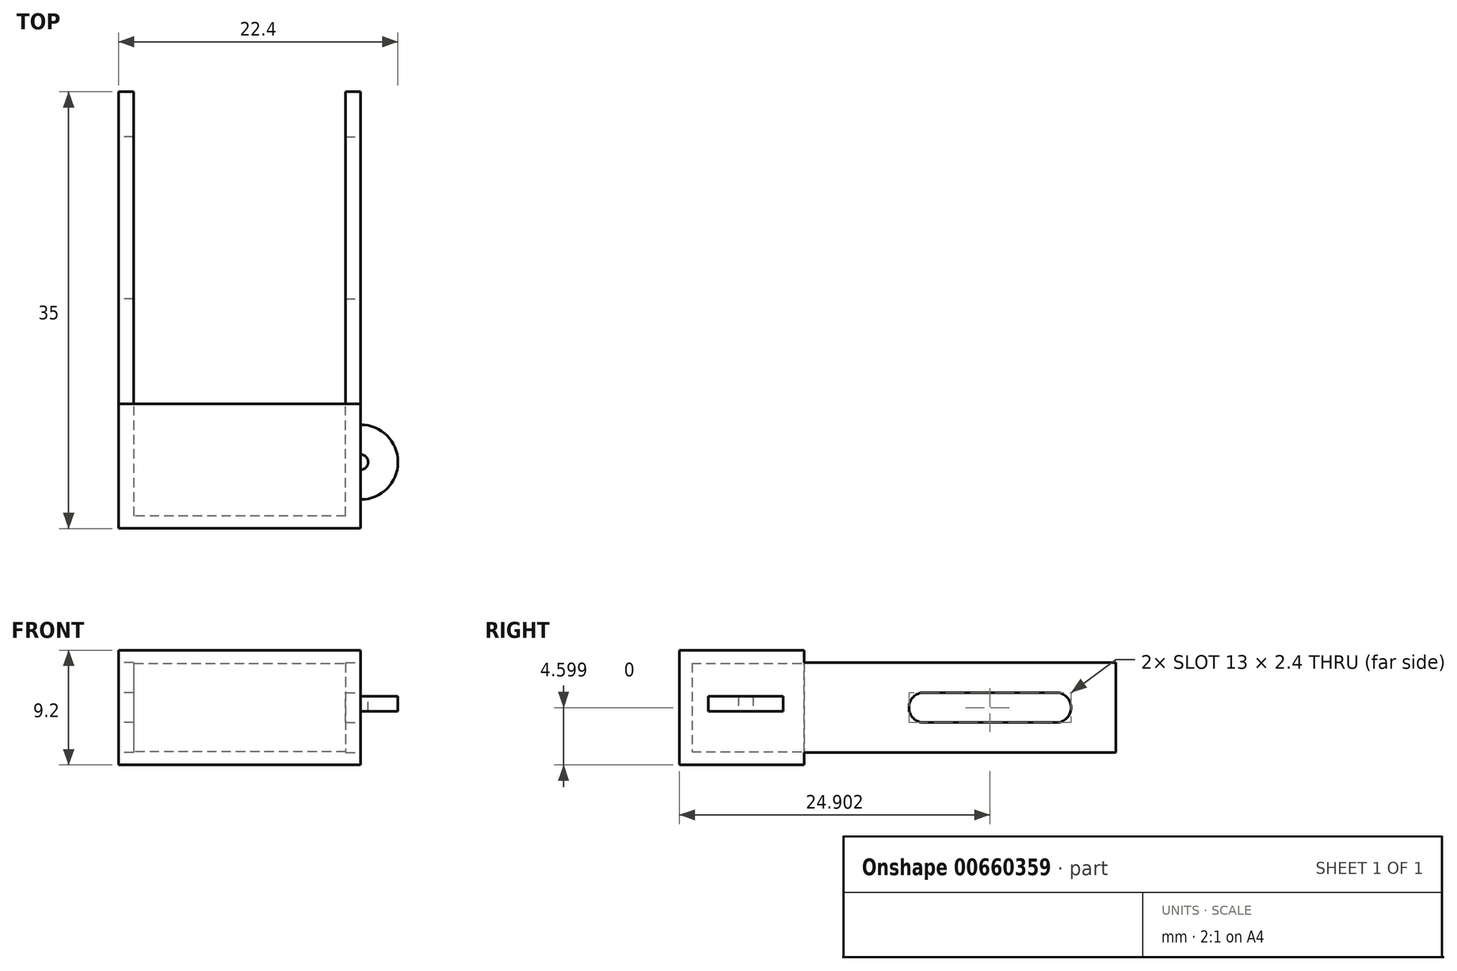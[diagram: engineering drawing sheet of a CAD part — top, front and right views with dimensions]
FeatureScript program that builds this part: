
annotation { "Feature Type Name" : "Feature", "Feature Type Description" : "" }
export const myFeature = defineFeature(function(context is Context, id is Id, definition is map)
    precondition{}
    {
        {
            var Q0;
            Q0=qCreatedBy(makeId("Right.planeOp"),FACE);
            var sketch = newSketch(context, id + "F0", { "sketchPlane" : qUnion([Q0])});
            skLineSegment(sketch, "E0.bottom", {"start": v(-18.67, 6.84) * mm, "end": v(-8.67, 6.84) * mm});
            skLineSegment(sketch, "E0.top", {"start": v(-18.67, -2.36) * mm, "end": v(-8.67, -2.36) * mm});
            skLineSegment(sketch, "E0.left", {"start": v(-18.67, 6.84) * mm, "end": v(-18.67, -2.36) * mm});
            skLineSegment(sketch, "E0.right", {"start": v(-8.67, 6.84) * mm, "end": v(-8.67, -2.36) * mm});
            skPoint(sketch, "E1", {"position": v(-8.67, 2.24) * mm});
            skLineSegment(sketch, "E2", {"start": v(-8.67, 2.24) * mm, "end": v(-8.67, 5.84) * mm});
            skLineSegment(sketch, "E3", {"start": v(-8.67, 5.84) * mm, "end": v(16.33, 5.84) * mm});
            skLineSegment(sketch, "E4", {"start": v(16.33, 5.84) * mm, "end": v(16.33, -1.36) * mm});
            skLineSegment(sketch, "E5", {"start": v(16.33, -1.36) * mm, "end": v(-8.67, -1.36) * mm});
            skLineSegment(sketch, "E6.top", {"start": v(-8.67, -1.36) * mm, "end": v(16.33, -1.36) * mm});
            skLineSegment(sketch, "E6.left", {"start": v(-8.67, 6.84) * mm, "end": v(-8.67, -1.36) * mm});
            skPoint(sketch, "E7", {"position": v(11.53, 2.24) * mm});
            skPoint(sketch, "E8", {"position": v(0.93, 2.24) * mm});
            skArc(sketch, "E9", {"start": v(11.53, 1.04) * mm, "mid": v(12.73, 2.24) * mm, "end": v(11.53, 3.44) * mm});
            skArc(sketch, "E10", {"start": v(0.93, 3.44) * mm, "mid": v(-0.27, 2.24) * mm, "end": v(0.93, 1.04) * mm});
            skLineSegment(sketch, "E11", {"start": v(0.93, 3.44) * mm, "end": v(11.53, 3.44) * mm});
            skLineSegment(sketch, "E12", {"start": v(11.53, 1.04) * mm, "end": v(0.93, 1.04) * mm});
            skSolve(sketch);
        }
        {
            var Q0;
            {var subQ1=sQuery(id+"F0.wireOp",EDGE,"E0.bottom");Q0=makeQuery(id+"F0.imprint","IMPRINT",FACE,{"disambiguationData":[TD([[makeQuery(id+"F0.imprint","IMPRINT",EDGE,{"derivedFrom":subQ1}),-1.0]])]});}
            extrude(context, id + "F1", {"entities" : qUnion([Q0]), "depth" : 19.4 * mm, "offsetDistance" : 25 * mm});
        }
        {
            var Q0;
            Q0=qSketchRegion(id+"F0",true);
            extrude(context, id + "F2", {"entities" : qUnion([Q0]), "operationType" : NewBodyOperationType.ADD, "depth" : 1.2 * mm, "offsetDistance" : 25 * mm});
        }
        {
            var Q0;
            Q0=makeQuery(id+"F1.opExtrude","CAP_FACE",FACE,{"disambiguationData":[OSD([sQuery(id+"F0.wireOp",EDGE,"E0.bottom"),sQuery(id+"F0.wireOp",EDGE,"E0.top"),sQuery(id+"F0.wireOp",EDGE,"E0.left"),sQuery(id+"F0.wireOp",EDGE,"E0.right"),sQuery(id+"F0.wireOp",EDGE,"E6.left")])],"isStart":false});
            var sketch = newSketch(context, id + "F3", { "sketchPlane" : qUnion([Q0])});
            skPoint(sketch, "E13", {"position": v(-8.67, 6.84) * mm});
            skPoint(sketch, "E14", {"position": v(-8.67, 5.84) * mm});
            skLineSegment(sketch, "E15", {"start": v(-8.67, 5.84) * mm, "end": v(16.33, 5.84) * mm});
            skLineSegment(sketch, "E16", {"start": v(16.33, 5.84) * mm, "end": v(16.33, -1.36) * mm});
            skLineSegment(sketch, "E17", {"start": v(16.33, -1.36) * mm, "end": v(-8.67, -1.36) * mm});
            skLineSegment(sketch, "E18", {"start": v(-8.67, -1.36) * mm, "end": v(-8.67, 5.84) * mm});
            skPoint(sketch, "E19", {"position": v(11.53, 2.24) * mm});
            skPoint(sketch, "E20", {"position": v(0.93, 2.24) * mm});
            skArc(sketch, "E21", {"start": v(11.53, 1.04) * mm, "mid": v(12.73, 2.24) * mm, "end": v(11.53, 3.44) * mm});
            skArc(sketch, "E22", {"start": v(0.93, 3.44) * mm, "mid": v(-0.27, 2.24) * mm, "end": v(0.93, 1.04) * mm});
            skLineSegment(sketch, "E23", {"start": v(11.53, 1.04) * mm, "end": v(0.93, 1.04) * mm});
            skLineSegment(sketch, "E24", {"start": v(0.93, 3.44) * mm, "end": v(11.53, 3.44) * mm});
            skSolve(sketch);
        }
        {
            var Q0;
            Q0=makeQuery(id+"F3.imprint","IMPRINT",FACE,{"disambiguationData":[TD([[makeQuery(id+"F3.imprint","IMPRINT",EDGE,{"derivedFrom":sQuery(id+"F3.wireOp",EDGE,"E15")}),-1.0]])]});
            extrude(context, id + "F4", {"entities" : qUnion([Q0]), "operationType" : NewBodyOperationType.ADD, "oppositeDirection" : true, "depth" : 1.2 * mm, "offsetDistance" : 25 * mm});
        }
        {
            var Q0;
            Q0=makeQuery(id+"F1.opExtrude","SWEPT_FACE",FACE,{"disambiguationData":[OSD([sQuery(id+"F0.wireOp",EDGE,"E0.right"),sQuery(id+"F0.wireOp",EDGE,"E6.left")])]});
            var sketch = newSketch(context, id + "F5", { "sketchPlane" : qUnion([Q0])});
            skLineSegment(sketch, "E25", {"start": v(-18.35, -1.31) * mm, "end": v(-1.25, -1.31) * mm});
            skLineSegment(sketch, "E26", {"start": v(-1.25, -1.31) * mm, "end": v(-1.25, 5.79) * mm});
            skLineSegment(sketch, "E27", {"start": v(-1.25, 5.79) * mm, "end": v(-18.35, 5.79) * mm});
            skLineSegment(sketch, "E28", {"start": v(-18.35, 5.79) * mm, "end": v(-18.35, -1.31) * mm});
            skSolve(sketch);
        }
        {
            var Q0;
            {var subQ0=sQuery(id+"F5.wireOp",EDGE,"E26");Q0=makeQuery(id+"F5.imprint","IMPRINT",FACE,{"disambiguationData":[TD([[makeQuery(id+"F5.imprint","IMPRINT",EDGE,{"derivedFrom":subQ0}),1.0]])]});}
            extrude(context, id + "F6", {"entities" : qUnion([Q0]), "operationType" : NewBodyOperationType.REMOVE, "oppositeDirection" : true, "depth" : 9 * mm, "offsetDistance" : 25 * mm});
        }
        {
            var Q0;
            Q0=makeQuery(id+"F4.boolean.opBoolean","MERGE",FACE,{"derivedFrom":[makeQuery(id+"F1.opExtrude","CAP_FACE",FACE,{"disambiguationData":[OSD([sQuery(id+"F0.wireOp",EDGE,"E0.bottom"),sQuery(id+"F0.wireOp",EDGE,"E0.top"),sQuery(id+"F0.wireOp",EDGE,"E0.left"),sQuery(id+"F0.wireOp",EDGE,"E0.right"),sQuery(id+"F0.wireOp",EDGE,"E6.left")])],"isStart":false}),makeQuery(id+"F4.opExtrude","CAP_FACE",FACE,{"disambiguationData":[OSD([sQuery(id+"F3.wireOp",EDGE,"E15"),sQuery(id+"F3.wireOp",EDGE,"E16"),sQuery(id+"F3.wireOp",EDGE,"E17"),sQuery(id+"F3.wireOp",EDGE,"E18"),sQuery(id+"F3.wireOp",EDGE,"9996f695-7c6a-4ae2-a82c-85ec2c8b4955"),sQuery(id+"F3.wireOp",EDGE,"aed22af8-8b87-41c4-a6d1-a50667118cd8"),sQuery(id+"F3.wireOp",EDGE,"3a73a6fe-88c4-49df-a490-4da8b549daf7"),sQuery(id+"F3.wireOp",EDGE,"59d502b7-973d-492e-8997-0d210c491a82"),sQuery(id+"F3.wireOp",EDGE,"dcc0dcc5-f484-47a7-98e3-21db19c0a036")])],"isStart":true})]});
            var sketch = newSketch(context, id + "F7", { "sketchPlane" : qUnion([Q0])});
            skLineSegment(sketch, "E29.bottom", {"start": v(-12.75, 3.14) * mm, "end": v(-10.35, 3.14) * mm});
            skLineSegment(sketch, "E29.top", {"start": v(-12.75, 1.94) * mm, "end": v(-10.35, 1.94) * mm});
            skLineSegment(sketch, "E29.left", {"start": v(-12.75, 3.14) * mm, "end": v(-12.75, 1.94) * mm});
            skLineSegment(sketch, "E29.right", {"start": v(-10.35, 3.14) * mm, "end": v(-10.35, 1.94) * mm});
            skLineSegment(sketch, "E30.bottom", {"start": v(-12.75, 3.14) * mm, "end": v(-13.35, 3.14) * mm});
            skLineSegment(sketch, "E30.top", {"start": v(-12.75, 1.94) * mm, "end": v(-13.35, 1.94) * mm});
            skLineSegment(sketch, "E30.right", {"start": v(-13.35, 3.14) * mm, "end": v(-13.35, 1.94) * mm});
            skLineSegment(sketch, "E31", {"start": v(-13.35, 3.14) * mm, "end": v(-13.35, 1.94) * mm, "construction": true});
            skSolve(sketch);
        }
        {
            var Q0;
            Q0=makeQuery(id+"F7.imprint","IMPRINT",FACE,{"disambiguationData":[TD([[makeQuery(id+"F7.imprint","IMPRINT",EDGE,{"derivedFrom":sQuery(id+"F7.wireOp",EDGE,"E29.bottom")}),-1.0]])]});
            var Q1;
            Q1=sQuery(id+"F7.wireOp",EDGE,"E30.right");
            revolve(context, id + "F8", {"operationType" : NewBodyOperationType.ADD, "entities" : qUnion([Q0]), "axis" : qUnion([Q1]), "revolveType" : RevolveType.ONE_DIRECTION, "angle" : 180 * degree});
        }
    });
